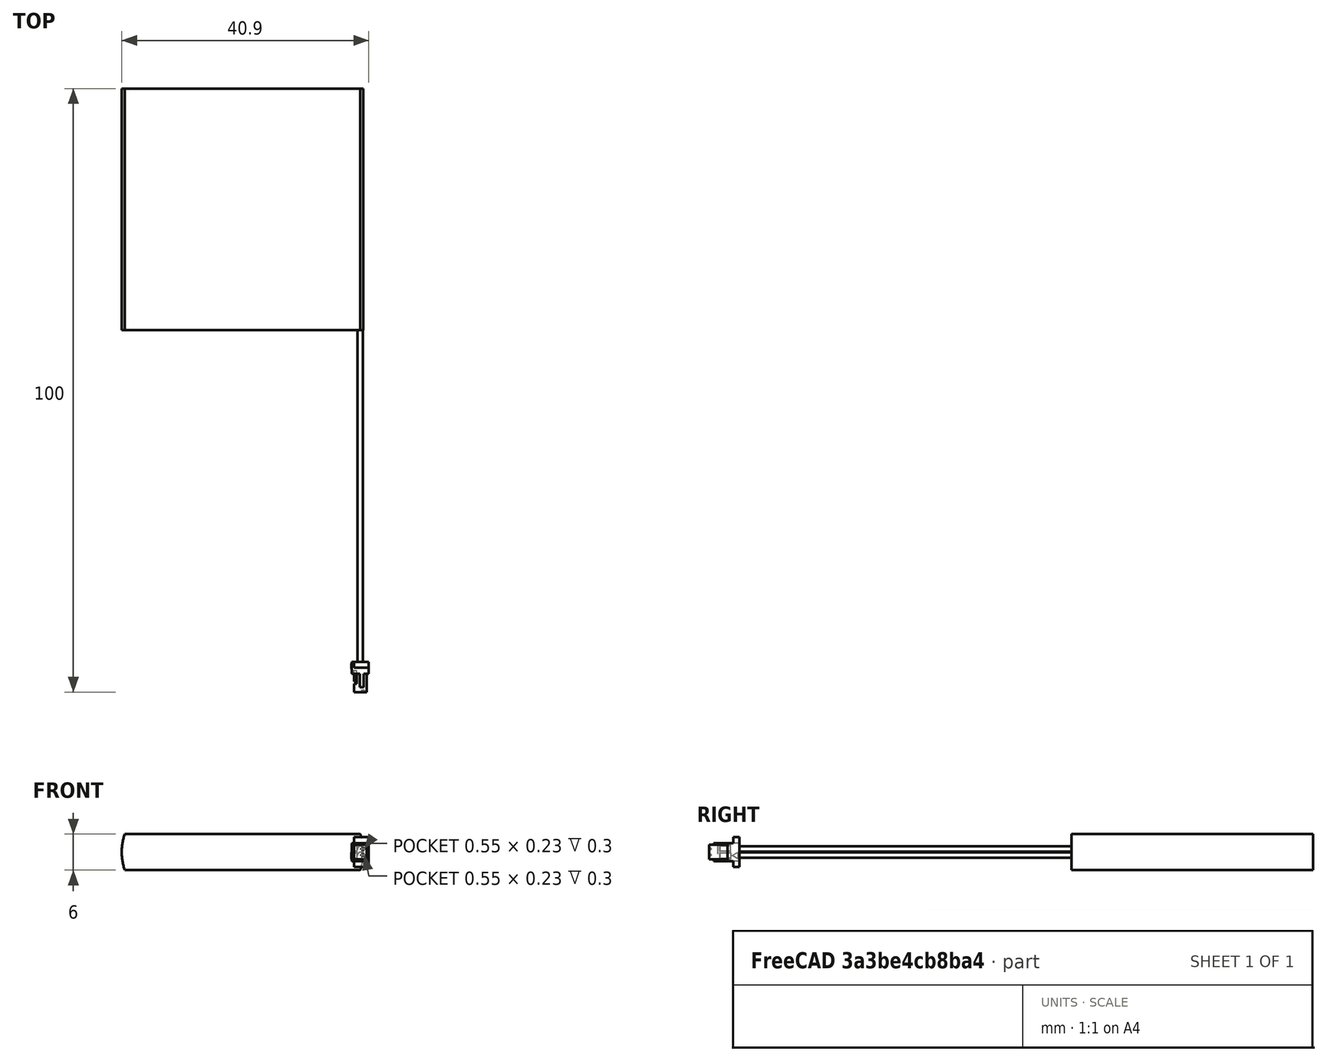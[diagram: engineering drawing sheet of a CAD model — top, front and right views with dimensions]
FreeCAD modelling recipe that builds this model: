
FCSTD DOCUMENT  (FreeCAD 2021.519R24301 +3652 (Git))
Label: ASR00008_1100mAh
License: Other
objects: TechDraw::DrawViewDimension×4, Sketcher::SketchObject×3, PartDesign::Pad×3, TechDraw::DrawViewPart×2, TechDraw::DrawViewAnnotation×2, PartDesign::Pocket×1, PartDesign::Mirrored×1, PartDesign::Body×1, Part::Feature×1, Part::MultiFuse×1, TechDraw::DrawSVGTemplate×1, TechDraw::DrawPage×1, Mesh::Feature×1
note: 21 computed .brp shape members not serialized (recipe doc carries the construction recipe); baked Part::Feature solids carry a one-line shape summary decoded from their .brp

FEATURE [Sketcher::SketchObject] Sketch
  FullyConstrained = true
  MapMode = 5
  Support = -> [XY_Plane]
  sketch-geometry (4):
    g0: LineSegment StartX=-20 StartY=20 StartZ=0 EndX=20 EndY=20 EndZ=0
    g1: LineSegment StartX=20 StartY=20 StartZ=0 EndX=20 EndY=-20 EndZ=0
    g2: LineSegment StartX=20 StartY=-20 StartZ=0 EndX=-20 EndY=-20 EndZ=0
    g3: LineSegment StartX=-20 StartY=-20 StartZ=0 EndX=-20 EndY=20 EndZ=0
  constraints (10):
    c: Coincident(g0,g1)
    c: Coincident(g1,g2)
    c: Coincident(g2,g3)
    c: Coincident(g3,g0)
    c: Horizontal(g2)
    c: Vertical(g1)
    c: Symmetric(g0,g2,g-1)
    c: Symmetric(g0,g0,g-2)
    c: DistanceX(g0,g0) = 40
    c: DistanceY(g3,g3) = 40
FEATURE [PartDesign::Pad] Pad
  ClaimChildren = false
  Direction = (1,1,1)
  Fit = 0
  FitJoin = 0
  InnerFit = 0
  InnerFitJoin = 0
  InnerTaperAngle = 0
  InnerTaperAngleRev = 0
  Length = 6
  Length2 = 100
  Midplane = true
  NewSolid = false
  Profile = -> Sketch
  Suppress = false
  Type = 0
FEATURE [Sketcher::SketchObject] Sketch001
  ExternalGeometry = -> [Pad]
  FullyConstrained = true
  MapMode = 5
  Placement = pos=(0,20,0) rot=(0,0.707107,0.707107;3.14159rad)
  Support = -> [Pad]
  sketch-geometry (5):
    g0: ArcOfCircle CenterX=-10.75 CenterY=-2.3e-15 CenterZ=0 NormalX=0 NormalY=0 NormalZ=1 AngleXU=0 Radius=9.25 StartAngle=2.8113 EndAngle=3.47189
    g1: LineSegment [constr] StartX=-19.5 StartY=-3 StartZ=0 EndX=-19.5 EndY=3 EndZ=0
    g2: LineSegment StartX=-19.5 StartY=-3 StartZ=0 EndX=-21 EndY=-3 EndZ=0
    g3: LineSegment StartX=-19.5 StartY=3 StartZ=0 EndX=-21 EndY=3 EndZ=0
    g4: LineSegment StartX=-21 StartY=3 StartZ=0 EndX=-21 EndY=-3 EndZ=0
  constraints (15):
    c: PointOnObject(g0,g-5)
    c: PointOnObject(g0,g-4)
    c: Tangent(g0,g-3)
    c: Coincident(g1,g0)
    c: Coincident(g1,g0)
    c: Vertical(g1)
    c: Coincident(g2,g0)
    c: Horizontal(g2)
    c: Coincident(g3,g0)
    c: Horizontal(g3)
    c: Coincident(g4,g3)
    c: Coincident(g4,g2)
    c: Vertical(g4)
    c: DistanceX(g3,g-4) = 1
    c: DistanceX(g-4,g0) = 0.5
FEATURE [PartDesign::Pocket] Pocket
  BaseFeature = -> Pad
  ClaimChildren = false
  Fit = 0
  FitJoin = 0
  InnerFit = 0
  InnerFitJoin = 0
  InnerTaperAngle = 0
  InnerTaperAngleRev = 0
  Length = 5
  Length2 = 100
  NewSolid = false
  Profile = -> Sketch001
  Suppress = false
  Type = 1
FEATURE [PartDesign::Mirrored] Mirrored
  BaseFeature = -> Pocket
  CopyShape = true
  MirrorPlane = -> Sketch001 [V_Axis]
  NewSolid = false
  OriginalSubs = -> [Pocket]
  Originals = -> [Pocket]
  ParallelTransform = true
  SubTransform = true
  Suppress = false
FEATURE [PartDesign::Pad] Pad001
  BaseFeature = -> Mirrored
  ClaimChildren = false
  Direction = (1,1,1)
  Fit = 0
  FitJoin = 0
  InnerFit = 0
  InnerFitJoin = 0
  InnerTaperAngle = 0
  InnerTaperAngleRev = 0
  Length = 7.85
  Length2 = 100
  NewSolid = false
  Profile = -> Mirrored [Face8]
  Reversed = true
  Suppress = false
  Type = 0
FEATURE [Sketcher::SketchObject] Sketch002
  ExternalGeometry = -> [Pad001]
  FullyConstrained = true
  MapMode = 5
  Placement = pos=(0,-20,0) rot=(1,0,0;1.5708rad)
  Support = -> [Pad001]
  sketch-geometry (7):
    g0: Circle CenterX=19.5 CenterY=-0.5 CenterZ=0 NormalX=0 NormalY=0 NormalZ=1 AngleXU=0 Radius=0.45
    g1: Circle CenterX=19.5 CenterY=0.5 CenterZ=0 NormalX=0 NormalY=0 NormalZ=1 AngleXU=0 Radius=0.45
    g2: LineSegment [constr] StartX=19.5 StartY=0.5 StartZ=0 EndX=19.5 EndY=-0.5 EndZ=0
    g3: GeomPoint [constr] X=19.5 Y=-0.95 Z=0
    g4: GeomPoint [constr] X=19.5 Y=0.95 Z=0
    g5: LineSegment [constr] StartX=19.05 StartY=-0.5 StartZ=0 EndX=19.95 EndY=-0.5 EndZ=0
    g6: GeomPoint [constr] X=19.5 Y=0.05 Z=0
  constraints (16):
    c: Coincident(g2,g1)
    c: Coincident(g2,g0)
    c: Equal(g0,g1)
    c: Diameter(g0) = 0.9
    c: Symmetric(g0,g1,g-1)
    c: PointOnObject(g3,g2)
    c: PointOnObject(g4,g1)
    c: Symmetric(g3,g4,g-1)
    c: PointOnObject(g5,g0)
    c: PointOnObject(g5,g0)
    c: Horizontal(g5)
    c: PointOnObject(g0,g5)
    c: PointOnObject(g6,g1)
    c: PointOnObject(g6,g2)
    c: DistanceX(g5,g-3) = 0.05
    c: DistanceY(g-3,g6) = 0.05
FEATURE [PartDesign::Pad] Pad002
  BaseFeature = -> Pad001
  ClaimChildren = false
  Direction = (1,1,1)
  Fit = 0
  FitJoin = 0
  InnerFit = 0
  InnerFitJoin = 0
  InnerTaperAngle = 0
  InnerTaperAngleRev = 0
  Length = 55
  Length2 = 100
  NewSolid = false
  Profile = -> Sketch002
  Suppress = false
  Type = 0
FEATURE [PartDesign::Body] Body
  AutoGroupSolids = false
  ExportMode = 0
  Group = -> [Sketch,Pad,Sketch001,Pocket,Mirrored,Pad001,Sketch002,Pad002]
  Origin = -> Origin
  Tip = -> Pad002
  _ExportChildren = -> [Pad,Pocket,Mirrored,Pad001,Pad002]
  _GroupVersion = 1
FEATURE [Part::Feature] Solid  label="Body007"
  Placement = pos=(18.2155,-77,1.45e-14) rot=(0,0,1;0rad)
  shape: bbox 2.9 x 5 x 4.94 mm, 60 faces (baked)
FEATURE [Part::MultiFuse] Fusion
  Shapes = -> [Body,Solid]
FEATURE [TechDraw::DrawSVGTemplate] Template
  Height = 210
  Orientation = 1
  Width = 297
FEATURE [TechDraw::DrawViewPart] View
  CoarseView = false
  Direction = (0,0,1)
  Focus = 100
  HardHidden = false
  IsoCount = 0
  IsoHidden = false
  IsoVisible = false
  LockPosition = false
  Perspective = false
  Rotation = 180
  Scale = 1.095
  ScaleType = 0
  SeamHidden = false
  SeamVisible = true
  SmoothHidden = false
  SmoothVisible = true
  Source = -> [Fusion]
  X = 178.5
  XDirection = (1,0,0)
  Y = 105
FEATURE [TechDraw::DrawViewPart] View001
  CoarseView = false
  Direction = (-1,0,0)
  Focus = 100
  HardHidden = false
  IsoCount = 0
  IsoHidden = false
  IsoVisible = false
  LockPosition = false
  Perspective = false
  Rotation = 90
  Scale = 1.095
  ScaleType = 0
  SeamHidden = false
  SeamVisible = true
  SmoothHidden = false
  SmoothVisible = true
  Source = -> [Fusion]
  X = 118.5
  XDirection = (0,-1,0)
  Y = 105
FEATURE [TechDraw::DrawViewDimension] Dimension
  Arbitrary = false
  ArbitraryTolerances = false
  EqualTolerance = true
  FormatSpec = %.1f
  FormatSpecOverTolerance = %+.1f
  FormatSpecUnderTolerance = %+.1f
  Inverted = false
  LockPosition = false
  MeasureType = 1
  OverTolerance = 0.5
  References2D = -> [View001]
  Rotation = 0
  ScaleType = 0
  TheoreticalExact = false
  Type = 1
  UnderTolerance = -0.5
  X = -32
  Y = -59
FEATURE [TechDraw::DrawViewDimension] Dimension001
  Arbitrary = false
  ArbitraryTolerances = false
  EqualTolerance = true
  FormatSpec = %.1f
  FormatSpecOverTolerance = %+.1f
  FormatSpecUnderTolerance = %+.1f
  Inverted = false
  LockPosition = false
  MeasureType = 1
  OverTolerance = 2
  References2D = -> [View]
  Rotation = 0
  ScaleType = 0
  TheoreticalExact = false
  Type = 1
  UnderTolerance = -2
  X = 39.4927
  Y = -59
FEATURE [TechDraw::DrawViewDimension] Dimension002
  Arbitrary = false
  ArbitraryTolerances = false
  EqualTolerance = true
  FormatSpec = %.1f
  FormatSpecOverTolerance = %+.1f
  FormatSpecUnderTolerance = %+.1f
  Inverted = false
  LockPosition = false
  MeasureType = 1
  OverTolerance = 3
  References2D = -> [View]
  Rotation = 0
  ScaleType = 0
  TheoreticalExact = false
  Type = 2
  UnderTolerance = -3
  X = -38
  Y = -31.85
FEATURE [TechDraw::DrawViewDimension] Dimension003
  Arbitrary = false
  ArbitraryTolerances = false
  EqualTolerance = true
  FormatSpec = %.1f
  FormatSpecOverTolerance = %+.1f
  FormatSpecUnderTolerance = %+.1f
  Inverted = false
  LockPosition = false
  MeasureType = 1
  OverTolerance = 5
  References2D = -> [View]
  Rotation = 0
  ScaleType = 0
  TheoreticalExact = false
  Type = 2
  UnderTolerance = -5
  X = -38
  Y = 20.1625
FEATURE [TechDraw::DrawViewAnnotation] Annotation
  Font = MS Shell Dlg 2
  LineSpace = 80
  LockPosition = false
  MaxWidth = -1
  Rotation = 0
  ScaleType = 0
  Text = SIDE VIEW
  TextSize = 6
  TextStyle = 0
  X = 118.5
  Y = 162
FEATURE [TechDraw::DrawViewAnnotation] Annotation001
  Font = MS Shell Dlg 2
  LineSpace = 80
  LockPosition = false
  MaxWidth = -1
  Rotation = 0
  ScaleType = 0
  Text = TOP VIEW
  TextSize = 5.99948
  TextStyle = 0
  X = 178.5
  Y = 162
FEATURE [TechDraw::DrawPage] Page
  KeepUpdated = true
  NextBalloonIndex = 1
  ProjectionType = 0
  Template = -> Template
  Views = -> [View,View001,Dimension,Dimension001,Dimension002,Dimension003,Annotation,Annotation001]
FEATURE [Mesh::Feature] Mesh  label="Fusion (Meshed)"
